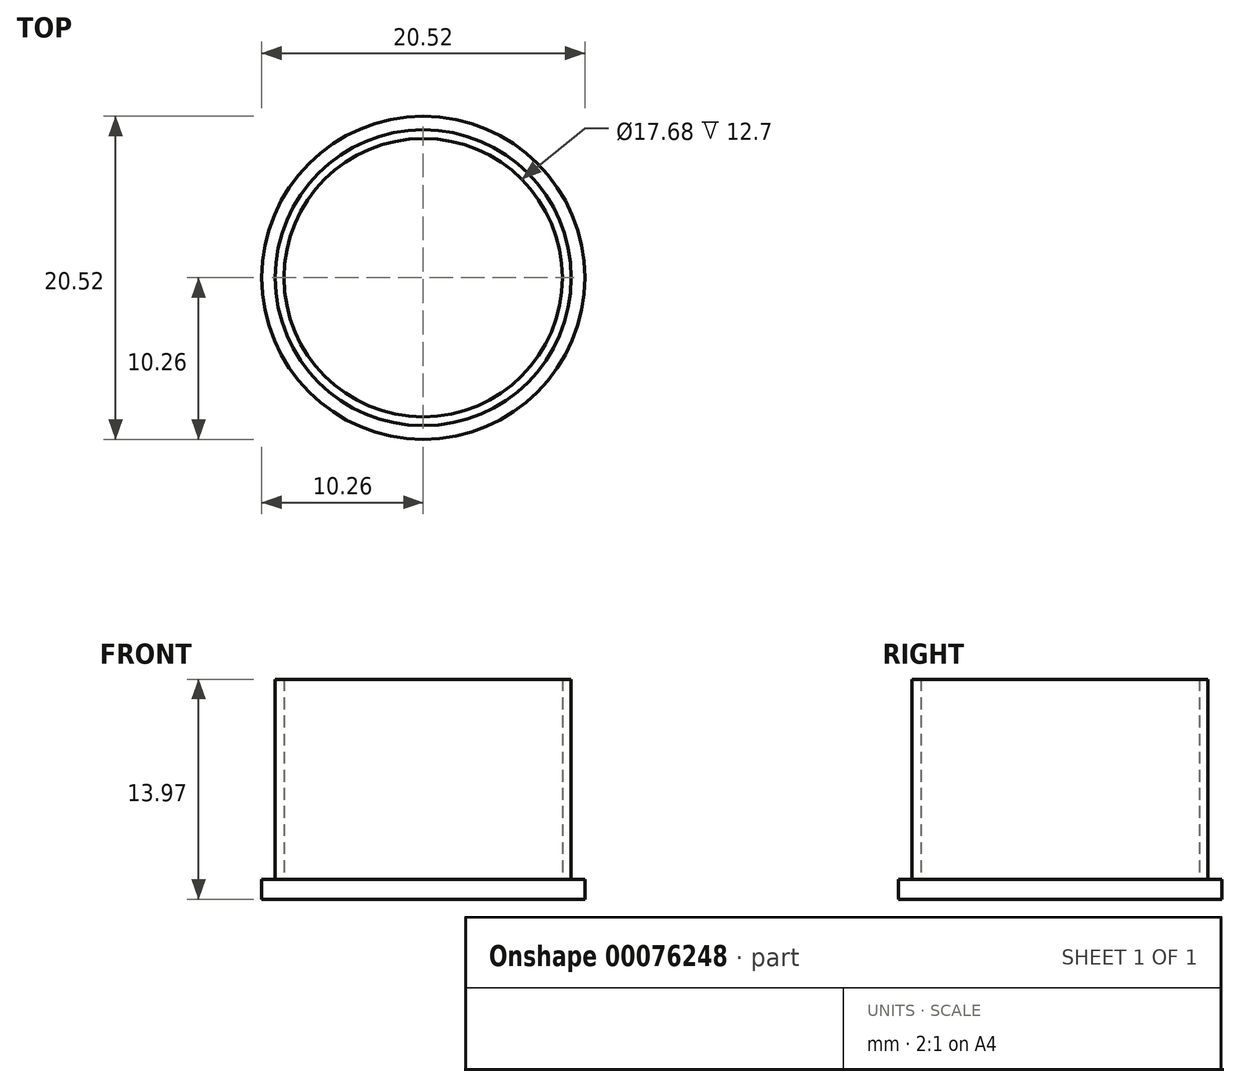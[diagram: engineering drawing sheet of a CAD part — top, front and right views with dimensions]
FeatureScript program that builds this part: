
annotation { "Feature Type Name" : "Feature", "Feature Type Description" : "" }
export const myFeature = defineFeature(function(context is Context, id is Id, definition is map)
    precondition{}
    {
        {
            var Q0;
            Q0=qCreatedBy(makeId("Top.planeOp"),FACE);
            var sketch = newSketch(context, id + "F0", { "sketchPlane" : qUnion([Q0])});
            skCircle(sketch, "E0", {"center": v(0, 0) * mm, "radius": 10.26 * mm});
            skSolve(sketch);
        }
        {
            var Q0;
            Q0 = qSketchRegion(id + "F0", true);
            extrude(context, id + "F1", {"entities" : qUnion([Q0]), "depth" : 1.27 * mm});
        }
        {
            var Q0;
            Q0=makeQuery(id+"F1.opExtrude","CAP_FACE",FACE,{"disambiguationData":[OSD([sQuery(id+"F0.wireOp",EDGE,"E0")])],"isStart":false});
            var sketch = newSketch(context, id + "F2", { "sketchPlane" : qUnion([Q0])});
            skCircle(sketch, "E1", {"center": v(0, 0) * mm, "radius": 9.4 * mm});
            skCircle(sketch, "E2", {"center": v(0, 0) * mm, "radius": 8.84 * mm});
            skSolve(sketch);
        }
        {
            var Q0;
            Q0=makeQuery(id+"F2.imprint","IMPRINT",FACE,{"disambiguationData":[TD([[makeQuery(id+"F2.imprint","IMPRINT",EDGE,{"derivedFrom":sQuery(id+"F2.wireOp",EDGE,"E1")}),1.0]])]});
            extrude(context, id + "F3", {"entities" : qUnion([Q0]), "operationType" : NewBodyOperationType.ADD, "depth" : 12.7 * mm});
        }
    });
